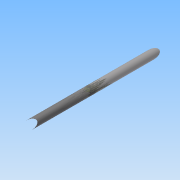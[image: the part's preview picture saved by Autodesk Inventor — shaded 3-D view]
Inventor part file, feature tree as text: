
AUTODESK INVENTOR PART (.ipt)
format: ipt  version: 2015 (Build 190159000, 159)  size: 88,576 bytes
history: native  units: mm
features: extrude x1, sketch x1
ambient origin geometry x8: Origin, YZ Plane, XZ Plane, XY Plane, X Axis, Y Axis, Z Axis, Center Point
bodies: Solid1 (feature_tree)
feature tree (2):
  extrude  "Extrusion1"  Depth=100.0mm TaperAngle=0.0deg
  sketch  "Sketch1"  dims[d0=5.0mm d1=100.0mm d2=0.0mm]
